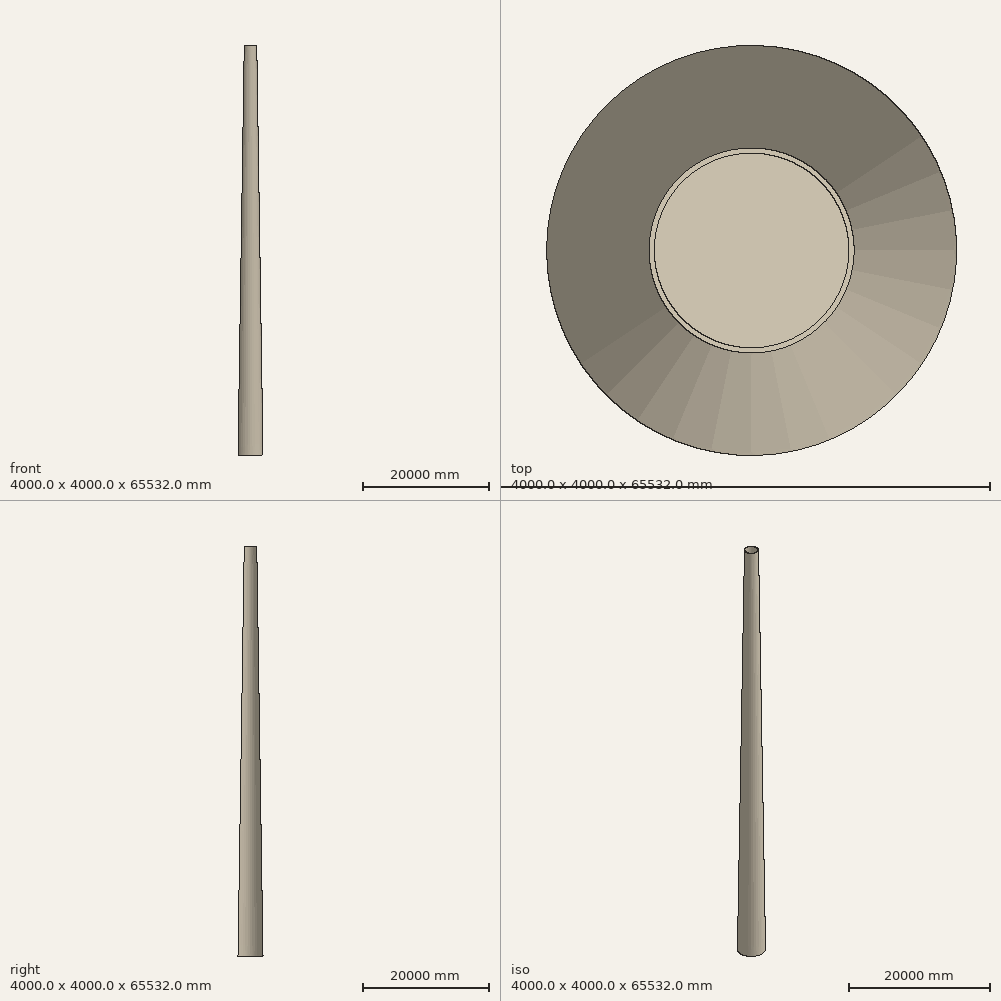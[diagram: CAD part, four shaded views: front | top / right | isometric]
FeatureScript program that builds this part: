
annotation { "Feature Type Name" : "Feature", "Feature Type Description" : "" }
export const myFeature = defineFeature(function(context is Context, id is Id, definition is map)
    precondition{}
    {
        {
            var Q0;
            Q0=qCreatedBy(makeId("Front.planeOp"),FACE);
            var sketch = newSketch(context, id + "F0", { "sketchPlane" : qUnion([Q0])});
            skLineSegment(sketch, "E0", {"start": v(0, 0) * mm, "end": v(-2000, 0) * mm});
            skLineSegment(sketch, "E1", {"start": v(-2000, 0) * mm, "end": v(-1000, 65532) * mm});
            skLineSegment(sketch, "E2", {"start": v(0, 0) * mm, "end": v(0, 65532) * mm});
            skLineSegment(sketch, "E3", {"start": v(0, 65532) * mm, "end": v(-1000, 65532) * mm});
            skSolve(sketch);
        }
        {
            var Q0;
            Q0=qSketchRegion(id+"F0",true);
            var Q1;
            Q1=sQuery(id+"F0.wireOp",EDGE,"E2");
            revolve(context, id + "F1", {"entities" : qUnion([Q0]), "axis" : qUnion([Q1]), "revolveType" : RevolveType.FULL});
        }
        {
            var Q0;
            Q0=makeQuery(id+"F1.opRevolve","SWEPT_FACE",FACE,{"disambiguationData":[OSD([sQuery(id+"F0.wireOp",EDGE,"E3")])]});
            shell(context, id + "F2", {"entities" : qUnion([Q0]), "thickness" : 50.8 * mm});
        }
    });
